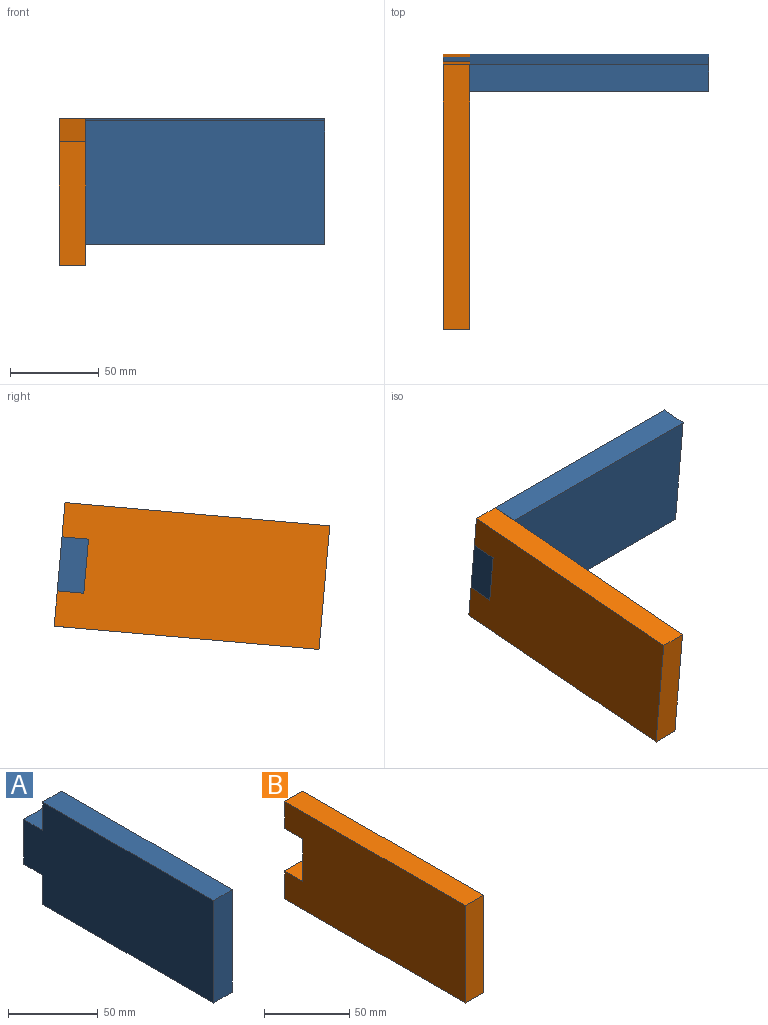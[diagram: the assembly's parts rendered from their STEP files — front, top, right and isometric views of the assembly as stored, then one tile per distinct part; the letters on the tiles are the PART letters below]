
ASSEMBLY  parts=2 mates=1
PART A: 10 faces, bbox 15x150x70 mm
  f0: plane 15x15mm, normal (0,0,1), area 225mm2, adj f1,f7,f8,f9
  f1: plane 19.39x15mm, normal (0,1,0), area 290.8mm2, adj f0,f2,f8,f9
  f2: plane 135x15mm, normal (0,0,1), area 2025mm2, adj f1,f3,f8,f9
  f3: plane 70x15mm, normal (0,-1,0), area 1050mm2, adj f2,f4,f8,f9
  f4: plane 135x15mm, normal (0,0,-1), area 2025mm2, adj f3,f5,f8,f9
  f5: plane 20x15mm, normal (0,1,0), area 300mm2, adj f4,f6,f8,f9
  f6: plane 15x15mm, normal (0,0,-1), area 225mm2, adj f5,f7,f8,f9
  f7: plane 30.61x15mm, normal (0,1,0), area 459.2mm2, adj f0,f6,f8,f9
  f8: plane 150x70mm, normal (1,0,0), area 9909.2mm2, adj f0,f1,f2,f3,f4,f5,f6,f7
  f9: plane 150x70mm, normal (-1,0,0), area 9909.2mm2, adj f0,f1,f2,f3,f4,f5,f6,f7
PART B: 10 faces, bbox 15x150x70 mm
  f0: plane 70x15mm, normal (0,-1,0), area 1050mm2, adj f1,f7,f8,f9
  f1: plane 150x15mm, normal (0,0,-1), area 2250mm2, adj f0,f2,f8,f9
  f2: plane 20x15mm, normal (0,1,0), area 300mm2, adj f1,f3,f8,f9
  f3: plane 15x15mm, normal (0,0,1), area 225mm2, adj f2,f4,f8,f9
  f4: plane 30.61x15mm, normal (0,1,0), area 459.2mm2, adj f3,f5,f8,f9
  f5: plane 15x15mm, normal (0,0,-1), area 225mm2, adj f4,f6,f8,f9
  f6: plane 19.39x15mm, normal (0,1,0), area 290.8mm2, adj f5,f7,f8,f9
  f7: plane 150x15mm, normal (0,0,1), area 2250mm2, adj f0,f6,f8,f9
  f8: plane 150x70mm, normal (1,0,0), area 10040.8mm2, adj f0,f1,f2,f3,f4,f5,f6,f7
  f9: plane 150x70mm, normal (-1,0,0), area 10040.8mm2, adj f0,f1,f2,f3,f4,f5,f6,f7
PLACE A rot(axis=(0.04,-0.04,1),90.1deg) t=(61.75,35.55,21.18)mm
PLACE B rot(axis=(1,0,0),5deg) t=(-18.6,-29.55,15.49)mm
MATE fastened B.f3 <-> A.f6  axis (0,-0.09,1) through (-11.1,44.43,5.8)mm
